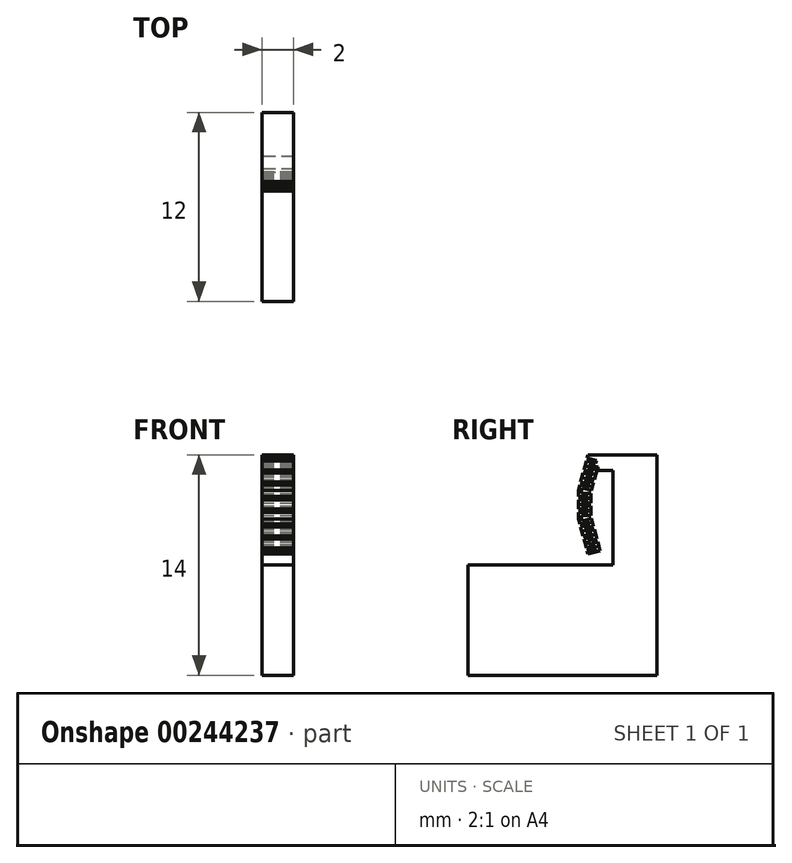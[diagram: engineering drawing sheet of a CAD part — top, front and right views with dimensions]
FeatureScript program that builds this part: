
annotation { "Feature Type Name" : "Feature", "Feature Type Description" : "" }
export const myFeature = defineFeature(function(context is Context, id is Id, definition is map)
    precondition{}
    {
        {
            assignVariable(context, id + "F0", {"name" : "thickness", "anyValue" : 2});
        }
        {
            var Q0;
            Q0=qCreatedBy(makeId("Right.planeOp"),FACE);
            var sketch = newSketch(context, id + "F1", { "sketchPlane" : qUnion([Q0])});
            skLineSegment(sketch, "E0", {"start": v(3.5, 0) * mm, "end": v(15.5, 0) * mm});
            skLineSegment(sketch, "E1", {"start": v(15.5, 0) * mm, "end": v(15.5, 14) * mm});
            skLineSegment(sketch, "E2", {"start": v(12.7, 7) * mm, "end": v(3.5, 7) * mm});
            skLineSegment(sketch, "E3", {"start": v(3.5, 7) * mm, "end": v(3.5, 0) * mm});
            skLineSegment(sketch, "E4", {"start": v(-9.03, 8.55) * mm, "end": v(17.3, 8.55) * mm, "construction": true});
            skLineSegment(sketch, "E5", {"start": v(15.5, 14) * mm, "end": v(11.1, 14) * mm});
            skLineSegment(sketch, "E6", {"start": v(11.1, 14) * mm, "end": v(10.5, 11.75) * mm});
            skLineSegment(sketch, "E7", {"start": v(10.5, 11.75) * mm, "end": v(10.5, 9.94) * mm});
            skLineSegment(sketch, "E8", {"start": v(10.5, 10.84) * mm, "end": v(13.6, 10.84) * mm, "construction": true});
            skLineSegment(sketch, "E9.MirrorCS", {"start": v(11.1, 7.69) * mm, "end": v(10.5, 9.94) * mm});
            skPoint(sketch, "E10", {"position": v(10.87, 8.55) * mm});
            skLineSegment(sketch, "E11.0", {"start": v(11.88, 7.9) * mm, "end": v(11.3, 10.04) * mm});
            skLineSegment(sketch, "E11.1", {"start": v(11.3, 11.64) * mm, "end": v(11.3, 10.04) * mm});
            skLineSegment(sketch, "E11.2", {"start": v(11.66, 13) * mm, "end": v(11.3, 11.64) * mm});
            skLineSegment(sketch, "E12", {"start": v(11.1, 7.69) * mm, "end": v(11.88, 7.9) * mm});
            skLineSegment(sketch, "E13", {"start": v(12.7, 7) * mm, "end": v(12.7, 13) * mm});
            skLineSegment(sketch, "E14", {"start": v(12.7, 13) * mm, "end": v(11.66, 13) * mm});
            skLineSegment(sketch, "E15", {"start": v(11.1, 14) * mm, "end": v(0, 14) * mm, "construction": true});
            skPoint(sketch, "E16", {"position": v(0, 7) * mm});
            skLineSegment(sketch, "E17.0", {"start": v(11.44, 7.99) * mm, "end": v(10.9, 10) * mm, "construction": true});
            skLineSegment(sketch, "E17.1", {"start": v(10.9, 11.7) * mm, "end": v(10.9, 10) * mm, "construction": true});
            skLineSegment(sketch, "E17.2", {"start": v(11.49, 13.9) * mm, "end": v(10.9, 11.7) * mm, "construction": true});
            skSolve(sketch);
        }
        {
            var Q0;
            Q0=qSketchRegion(id+"F1",true);
            extrude(context, id + "F2", {"entities" : qUnion([Q0]), "endBound" : BoundingType.SYMMETRIC, "depth" : (getVariable(context, 'thickness')) * mm});
        }
        {
            var Q0;
            Q0=qCreatedBy(makeId("Right.planeOp"),FACE);
            var sketch = newSketch(context, id + "F3", { "sketchPlane" : qUnion([Q0])});
            skLineSegment(sketch, "E18", {"start": v(0, 0) * mm, "end": v(0, 7) * mm, "construction": true});
            skPoint(sketch, "E19", {"position": v(0, 7) * mm});
            skSolve(sketch);
        }
        {
            var Q0;
            Q0=makeQuery(id+"F2.opExtrude","CAP_FACE",FACE,{"disambiguationData":[OSD([sQuery(id+"F1.wireOp",EDGE,"E0"),sQuery(id+"F1.wireOp",EDGE,"E1"),sQuery(id+"F1.wireOp",EDGE,"E2"),sQuery(id+"F1.wireOp",EDGE,"E3"),sQuery(id+"F1.wireOp",EDGE,"E5"),sQuery(id+"F1.wireOp",EDGE,"E6"),sQuery(id+"F1.wireOp",EDGE,"E7"),sQuery(id+"F1.wireOp",EDGE,"E9.MirrorCS"),sQuery(id+"F1.wireOp",EDGE,"E11.0"),sQuery(id+"F1.wireOp",EDGE,"E11.1"),sQuery(id+"F1.wireOp",EDGE,"E11.2"),sQuery(id+"F1.wireOp",EDGE,"E12"),sQuery(id+"F1.wireOp",EDGE,"E13"),sQuery(id+"F1.wireOp",EDGE,"E14")])],"isStart":false});
            var sketch = newSketch(context, id + "F4", { "sketchPlane" : qUnion([Q0])});
            skLineSegment(sketch, "E20", {"start": v(11, 8.08) * mm, "end": v(11.58, 8.23) * mm});
            skLineSegment(sketch, "E21", {"start": v(11.58, 8.23) * mm, "end": v(11.63, 8.04) * mm});
            skLineSegment(sketch, "E22", {"start": v(11.63, 8.04) * mm, "end": v(11.05, 7.88) * mm});
            skLineSegment(sketch, "E23", {"start": v(11.05, 7.88) * mm, "end": v(11, 8.08) * mm});
            skLineSegment(sketch, "E24", {"start": v(11.72, 8.48) * mm, "end": v(11.14, 8.32) * mm});
            skLineSegment(sketch, "E25", {"start": v(11.14, 8.32) * mm, "end": v(11.09, 8.51) * mm});
            skLineSegment(sketch, "E26", {"start": v(11.09, 8.51) * mm, "end": v(11.67, 8.67) * mm});
            skLineSegment(sketch, "E27", {"start": v(11.67, 8.67) * mm, "end": v(11.72, 8.48) * mm});
            skLineSegment(sketch, "E28.1.0.0", {"start": v(11.42, 8.81) * mm, "end": v(10.84, 8.65) * mm});
            skLineSegment(sketch, "E28.1.0.1", {"start": v(11.37, 9) * mm, "end": v(11.42, 8.81) * mm});
            skLineSegment(sketch, "E28.1.0.2", {"start": v(10.93, 9.1) * mm, "end": v(10.88, 9.29) * mm});
            skLineSegment(sketch, "E28.1.0.3", {"start": v(10.84, 8.65) * mm, "end": v(10.8, 8.85) * mm});
            skLineSegment(sketch, "E28.1.0.4", {"start": v(11.51, 9.25) * mm, "end": v(10.93, 9.1) * mm});
            skLineSegment(sketch, "E28.1.0.5", {"start": v(10.8, 8.85) * mm, "end": v(11.37, 9) * mm});
            skLineSegment(sketch, "E28.1.0.6", {"start": v(10.88, 9.29) * mm, "end": v(11.46, 9.44) * mm});
            skLineSegment(sketch, "E28.1.0.7", {"start": v(11.46, 9.44) * mm, "end": v(11.51, 9.25) * mm});
            skLineSegment(sketch, "E28.2.0.0", {"start": v(11.22, 9.58) * mm, "end": v(10.64, 9.43) * mm});
            skLineSegment(sketch, "E28.2.0.1", {"start": v(11.16, 9.78) * mm, "end": v(11.22, 9.58) * mm});
            skLineSegment(sketch, "E28.2.0.3", {"start": v(10.64, 9.43) * mm, "end": v(10.59, 9.62) * mm});
            skLineSegment(sketch, "E28.2.0.5", {"start": v(10.59, 9.62) * mm, "end": v(11.16, 9.78) * mm});
            skLineSegment(sketch, "E28.direction1", {"start": v(11.05, 7.88) * mm, "end": v(10.84, 8.65) * mm, "construction": true});
            skLineSegment(sketch, "E29", {"start": v(11.3, 10.14) * mm, "end": v(10.7, 10.14) * mm});
            skLineSegment(sketch, "E30", {"start": v(10.5, 9.94) * mm, "end": v(11.3, 10.04) * mm, "construction": true});
            skLineSegment(sketch, "E31.MirrorCS", {"start": v(11.33, 9.95) * mm, "end": v(10.75, 9.8) * mm});
            skLineSegment(sketch, "E32", {"start": v(10.5, 10.14) * mm, "end": v(10.5, 9.94) * mm, "construction": true});
            skLineSegment(sketch, "E33", {"start": v(10.5, 9.94) * mm, "end": v(10.55, 9.74) * mm, "construction": true});
            skLineSegment(sketch, "E34.0", {"start": v(10.7, 9.97) * mm, "end": v(10.75, 9.8) * mm});
            skLineSegment(sketch, "E34.1", {"start": v(10.7, 10.14) * mm, "end": v(10.7, 9.97) * mm});
            skLineSegment(sketch, "E35", {"start": v(11.3, 10.14) * mm, "end": v(11.3, 10.04) * mm});
            skLineSegment(sketch, "E36", {"start": v(11.3, 10.04) * mm, "end": v(11.33, 9.95) * mm});
            skLineSegment(sketch, "E37", {"start": v(10.5, 10.84) * mm, "end": v(11.9, 10.84) * mm, "construction": true});
            skLineSegment(sketch, "E38", {"start": v(10.5, 10.34) * mm, "end": v(11.1, 10.34) * mm});
            skLineSegment(sketch, "E39", {"start": v(11.1, 10.34) * mm, "end": v(11.1, 10.54) * mm});
            skLineSegment(sketch, "E40", {"start": v(11.1, 10.54) * mm, "end": v(10.5, 10.54) * mm});
            skLineSegment(sketch, "E41", {"start": v(10.5, 10.54) * mm, "end": v(10.5, 10.34) * mm});
            skLineSegment(sketch, "E42", {"start": v(11.3, 10.74) * mm, "end": v(10.7, 10.74) * mm});
            skLineSegment(sketch, "E43", {"start": v(10.7, 10.74) * mm, "end": v(10.7, 10.84) * mm});
            skLineSegment(sketch, "E44", {"start": v(11.3, 10.74) * mm, "end": v(11.3, 10.84) * mm});
            skLineSegment(sketch, "E45.MirrorCS", {"start": v(11.05, 13.8) * mm, "end": v(11, 13.61) * mm});
            skLineSegment(sketch, "E46.MirrorCS", {"start": v(11.3, 10.94) * mm, "end": v(11.3, 10.84) * mm});
            skLineSegment(sketch, "E47.MirrorCS", {"start": v(11.16, 11.91) * mm, "end": v(11.22, 12.1) * mm});
            skLineSegment(sketch, "E48.MirrorCS", {"start": v(11.1, 11.14) * mm, "end": v(10.5, 11.14) * mm});
            skLineSegment(sketch, "E49.MirrorCS", {"start": v(10.93, 12.6) * mm, "end": v(10.88, 12.4) * mm});
            skLineSegment(sketch, "E50.MirrorCS", {"start": v(10.5, 11.14) * mm, "end": v(10.5, 11.34) * mm});
            skLineSegment(sketch, "E51.MirrorCS", {"start": v(10.88, 12.4) * mm, "end": v(11.46, 12.25) * mm});
            skLineSegment(sketch, "E52.MirrorCS", {"start": v(11.37, 12.69) * mm, "end": v(11.42, 12.88) * mm});
            skLineSegment(sketch, "E53.MirrorCS", {"start": v(11.1, 11.34) * mm, "end": v(11.1, 11.14) * mm});
            skLineSegment(sketch, "E54.MirrorCS", {"start": v(10.84, 13.03) * mm, "end": v(10.8, 12.84) * mm});
            skLineSegment(sketch, "E55.MirrorCS", {"start": v(11.58, 13.46) * mm, "end": v(11.63, 13.65) * mm});
            skLineSegment(sketch, "E56.MirrorCS", {"start": v(11.42, 12.88) * mm, "end": v(10.84, 13.03) * mm});
            skLineSegment(sketch, "E57.MirrorCS", {"start": v(11.14, 13.37) * mm, "end": v(11.09, 13.18) * mm});
            skLineSegment(sketch, "E58.MirrorCS", {"start": v(11.22, 12.1) * mm, "end": v(10.64, 12.26) * mm});
            skLineSegment(sketch, "E59.MirrorCS", {"start": v(11.3, 11.54) * mm, "end": v(11.3, 11.64) * mm});
            skLineSegment(sketch, "E60.MirrorCS", {"start": v(10.59, 12.07) * mm, "end": v(11.16, 11.91) * mm});
            skLineSegment(sketch, "E61.MirrorCS", {"start": v(10.64, 12.26) * mm, "end": v(10.59, 12.07) * mm});
            skLineSegment(sketch, "E62.MirrorCS", {"start": v(11.63, 13.65) * mm, "end": v(11.05, 13.8) * mm});
            skLineSegment(sketch, "E63.MirrorCS", {"start": v(11, 13.61) * mm, "end": v(11.58, 13.46) * mm});
            skLineSegment(sketch, "E64.MirrorCS", {"start": v(10.7, 11.72) * mm, "end": v(10.75, 11.9) * mm});
            skLineSegment(sketch, "E65.MirrorCS", {"start": v(11.3, 10.94) * mm, "end": v(10.7, 10.94) * mm});
            skLineSegment(sketch, "E66.MirrorCS", {"start": v(10.7, 10.94) * mm, "end": v(10.7, 10.84) * mm});
            skLineSegment(sketch, "E67.MirrorCS", {"start": v(10.5, 11.34) * mm, "end": v(11.1, 11.34) * mm});
            skLineSegment(sketch, "E68.MirrorCS", {"start": v(11.3, 11.54) * mm, "end": v(10.7, 11.54) * mm});
            skLineSegment(sketch, "E69.MirrorCS", {"start": v(11.51, 12.44) * mm, "end": v(10.93, 12.6) * mm});
            skLineSegment(sketch, "E70.MirrorCS", {"start": v(11.3, 11.64) * mm, "end": v(11.33, 11.74) * mm});
            skLineSegment(sketch, "E71.MirrorCS", {"start": v(11.09, 13.18) * mm, "end": v(11.66, 13.02) * mm});
            skLineSegment(sketch, "E72.MirrorCS", {"start": v(10.7, 11.54) * mm, "end": v(10.7, 11.72) * mm});
            skLineSegment(sketch, "E73.MirrorCS", {"start": v(11.33, 11.74) * mm, "end": v(10.75, 11.9) * mm});
            skLineSegment(sketch, "E74.MirrorCS", {"start": v(11.72, 13.21) * mm, "end": v(11.14, 13.37) * mm});
            skLineSegment(sketch, "E75.MirrorCS", {"start": v(10.8, 12.84) * mm, "end": v(11.37, 12.69) * mm});
            skLineSegment(sketch, "E76.MirrorCS", {"start": v(11.46, 12.25) * mm, "end": v(11.51, 12.44) * mm});
            skLineSegment(sketch, "E77", {"start": v(11.72, 13.21) * mm, "end": v(11.72, 13) * mm});
            skLineSegment(sketch, "E78", {"start": v(11.72, 13) * mm, "end": v(11.66, 13) * mm});
            skLineSegment(sketch, "E79", {"start": v(11.66, 13) * mm, "end": v(11.66, 13.02) * mm});
            skSolve(sketch);
        }
        {
            var Q0;
            Q0=qSketchRegion(id+"F4",true);
            extrude(context, id + "F5", {"entities" : qUnion([Q0]), "operationType" : NewBodyOperationType.REMOVE, "endBound" : BoundingType.UP_TO_NEXT, "oppositeDirection" : true, "depth" : 25 * mm});
        }
    });
